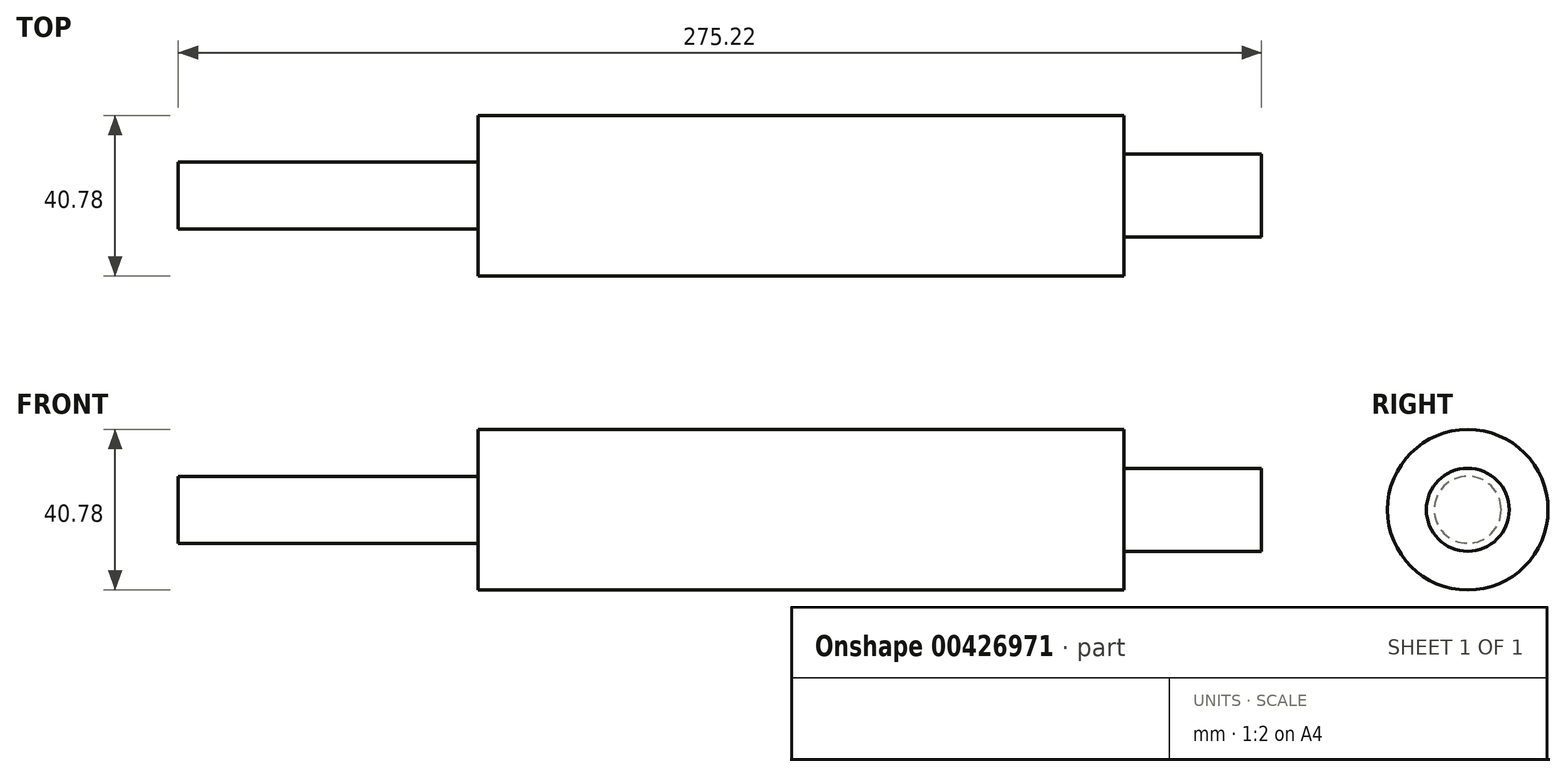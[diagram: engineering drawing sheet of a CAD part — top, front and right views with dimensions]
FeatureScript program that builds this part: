
annotation { "Feature Type Name" : "Feature", "Feature Type Description" : "" }
export const myFeature = defineFeature(function(context is Context, id is Id, definition is map)
    precondition{}
    {
        {
            var Q0;
            Q0=qCreatedBy(makeId("Front.planeOp"),FACE);
            var sketch = newSketch(context, id + "F0", { "sketchPlane" : qUnion([Q0])});
            skLineSegment(sketch, "E0", {"start": v(-177.5, 0) * mm, "end": v(173.47, 0) * mm, "construction": true});
            skLineSegment(sketch, "E1", {"start": v(-54.24, 0) * mm, "end": v(-54.24, 20.4) * mm});
            skLineSegment(sketch, "E2", {"start": v(-54.24, 20.4) * mm, "end": v(33.62, 20.4) * mm});
            skLineSegment(sketch, "E3", {"start": v(33.62, 0) * mm, "end": v(-54.24, 0) * mm});
            skLineSegment(sketch, "E4", {"start": v(33.62, 20.4) * mm, "end": v(33.62, 10.53) * mm});
            skLineSegment(sketch, "E5", {"start": v(33.62, 10.53) * mm, "end": v(68.58, 10.53) * mm});
            skLineSegment(sketch, "E6", {"start": v(68.58, 10.53) * mm, "end": v(68.58, 0) * mm});
            skLineSegment(sketch, "E7", {"start": v(68.58, 0) * mm, "end": v(33.62, 0) * mm});
            skSolve(sketch);
        }
        {
            var Q0;
            Q0=makeQuery(id+"F0.imprint","IMPRINT",FACE,{"disambiguationData":[TD([[makeQuery(id+"F0.imprint","IMPRINT",EDGE,{"derivedFrom":sQuery(id+"F0.wireOp",EDGE,"E1")}),-1.0]])]});
            var Q1;
            Q1=sQuery(id+"F0.wireOp",EDGE,"E0");
            revolve(context, id + "F1", {"entities" : qUnion([Q0]), "axis" : qUnion([Q1]), "revolveType" : RevolveType.FULL});
        }
        {
            var Q0;
            Q0=qCreatedBy(makeId("Right.planeOp"),FACE);
            var sketch = newSketch(context, id + "F2", { "sketchPlane" : qUnion([Q0])});
            skCircle(sketch, "E8", {"center": v(0, 0) * mm, "radius": 10.74 * mm});
            skSolve(sketch);
        }
        {
            var Q0;
            Q0 = qSketchRegion(id + "F2", true);
            var Q1;
            Q1=makeQuery(id+"F1.opRevolve","SWEPT_FACE",FACE,{"disambiguationData":[OSD([sQuery(id+"F0.wireOp",EDGE,"E1")])]});
            extrude(context, id + "F3", {"entities" : qUnion([Q0, Q1]), "operationType" : NewBodyOperationType.ADD, "oppositeDirection" : true, "depth" : 76.2 * mm});
        }
        {
            var Q0;
            Q0=makeQuery(id+"F3.opExtrude","CAP_FACE",FACE,{"disambiguationData":[OSD([sQuery(id+"F0.wireOp",EDGE,"E1")])],"isStart":false});
            var sketch = newSketch(context, id + "F4", { "sketchPlane" : qUnion([Q0])});
            skCircle(sketch, "E9", {"center": v(0, 0) * mm, "radius": 8.5 * mm});
            skSolve(sketch);
        }
        {
            var Q0;
            Q0=makeQuery(id+"F4.imprint","IMPRINT",FACE,{"disambiguationData":[TD([[makeQuery(id+"F4.imprint","IMPRINT",EDGE,{"derivedFrom":sQuery(id+"F4.wireOp",EDGE,"E9")}),1.0]])]});
            extrude(context, id + "F5", {"entities" : qUnion([Q0]), "operationType" : NewBodyOperationType.ADD, "depth" : 76.2 * mm});
        }
    });
